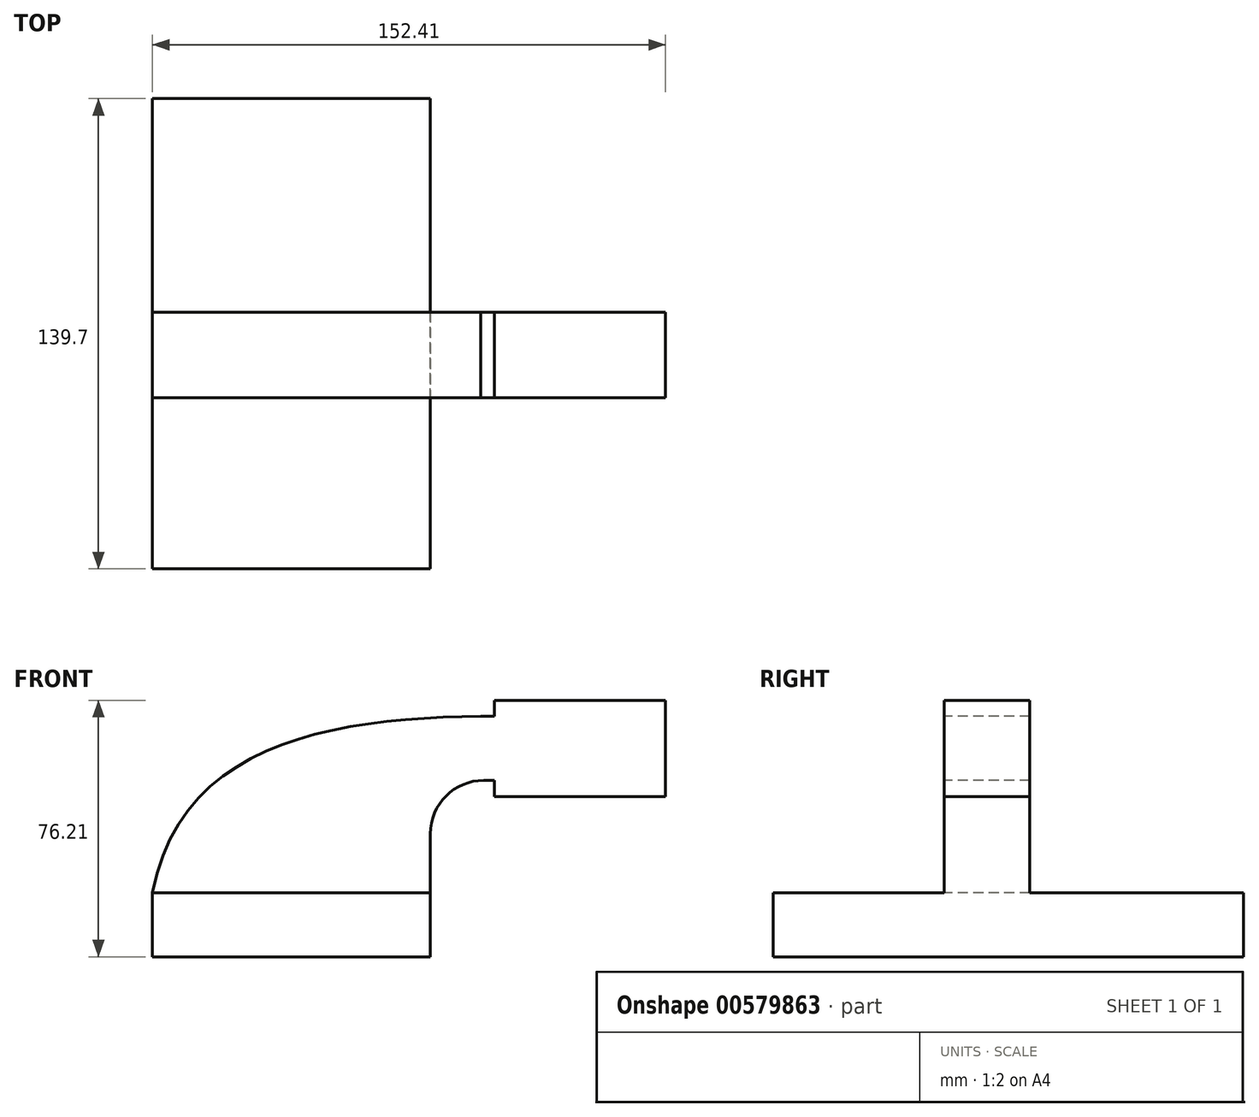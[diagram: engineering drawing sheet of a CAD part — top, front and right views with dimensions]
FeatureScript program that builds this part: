
annotation { "Feature Type Name" : "Feature", "Feature Type Description" : "" }
export const myFeature = defineFeature(function(context is Context, id is Id, definition is map)
    precondition{}
    {
        {
            var Q0;
            Q0=qCreatedBy(makeId("Front.planeOp"),FACE);
            var sketch = newSketch(context, id + "F0", { "sketchPlane" : qUnion([Q0])});
            skLineSegment(sketch, "E0.bottom", {"start": v(41.28, -9.52) * mm, "end": v(-41.27, -9.53) * mm});
            skLineSegment(sketch, "E0.top", {"start": v(41.27, 9.53) * mm, "end": v(-41.28, 9.53) * mm});
            skLineSegment(sketch, "E0.left", {"start": v(41.28, -9.52) * mm, "end": v(41.28, 9.53) * mm});
            skLineSegment(sketch, "E0.right", {"start": v(-41.27, -9.53) * mm, "end": v(-41.28, 9.53) * mm});
            skPoint(sketch, "E0.middle", {"position": v(0, 0) * mm});
            skLineSegment(sketch, "E1.bottom", {"start": v(111.12, 38.1) * mm, "end": v(60.32, 38.1) * mm});
            skLineSegment(sketch, "E1.top", {"start": v(111.12, 66.68) * mm, "end": v(60.32, 66.68) * mm});
            skLineSegment(sketch, "E1.left", {"start": v(111.12, 38.1) * mm, "end": v(111.12, 66.68) * mm});
            skLineSegment(sketch, "E1.right", {"start": v(60.32, 38.1) * mm, "end": v(60.32, 66.68) * mm});
            skPoint(sketch, "E1.middle", {"position": v(85.72, 52.39) * mm});
            skLineSegment(sketch, "E2", {"start": v(41.27, 9.53) * mm, "end": v(41.27, 27) * mm});
            skArc(sketch, "E3", {"start": v(41.27, 27) * mm, "mid": v(45.92, 38.23) * mm, "end": v(57.15, 42.88) * mm});
            skLineSegment(sketch, "E4", {"start": v(57.15, 42.88) * mm, "end": v(85.72, 42.88) * mm});
            skLineSegment(sketch, "E5.0", {"start": v(57.15, 61.93) * mm, "end": v(85.72, 61.93) * mm});
            skArc(sketch, "E5.1", {"start": v(22.23, 27) * mm, "mid": v(32.45, 51.7) * mm, "end": v(57.15, 61.93) * mm});
            skLineSegment(sketch, "E5.2", {"start": v(22.22, 9.53) * mm, "end": v(22.22, 27) * mm});
            skLineSegment(sketch, "E6", {"start": v(85.72, 66.67) * mm, "end": v(85.72, 38.1) * mm});
            skFitSpline(sketch, "E7", {"points": [v(-41.28, 9.52) * mm, v(57.15, 61.93) * mm], "startDerivative": vector(26.12, 136.92) * mm, "endDerivative": vector(128.96, 1.51) * mm});
            skSolve(sketch);
        }
        {
            var Q0;
            Q0=makeQuery(id+"F0.imprint","IMPRINT",FACE,{"disambiguationData":[TD([[makeQuery(id+"F0.imprint","IMPRINT",EDGE,{"derivedFrom":sQuery(id+"F0.wireOp",EDGE,"E0.bottom")}),-1.0]])]});
            extrude(context, id + "F1", {"entities" : qUnion([Q0]), "endBound" : BoundingType.SYMMETRIC, "depth" : 127 * mm, "offsetDistance" : 25.4 * mm});
        }
        {
            var Q0;
            Q0=makeQuery(id+"F1.opExtrude","CAP_FACE",FACE,{"disambiguationData":[OSD([sQuery(id+"F0.wireOp",EDGE,"E0.bottom"),sQuery(id+"F0.wireOp",EDGE,"E0.top"),sQuery(id+"F0.wireOp",EDGE,"E0.left"),sQuery(id+"F0.wireOp",EDGE,"E0.right")])],"isStart":true});
            var Q1;
            Q1 = qSketchRegion(id + "F0", true);
            extrude(context, id + "F2", {"entities" : qUnion([Q0, Q1]), "operationType" : NewBodyOperationType.ADD, "endBound" : BoundingType.SYMMETRIC, "depth" : 25.4 * mm, "offsetDistance" : 25.4 * mm});
        }
    });
